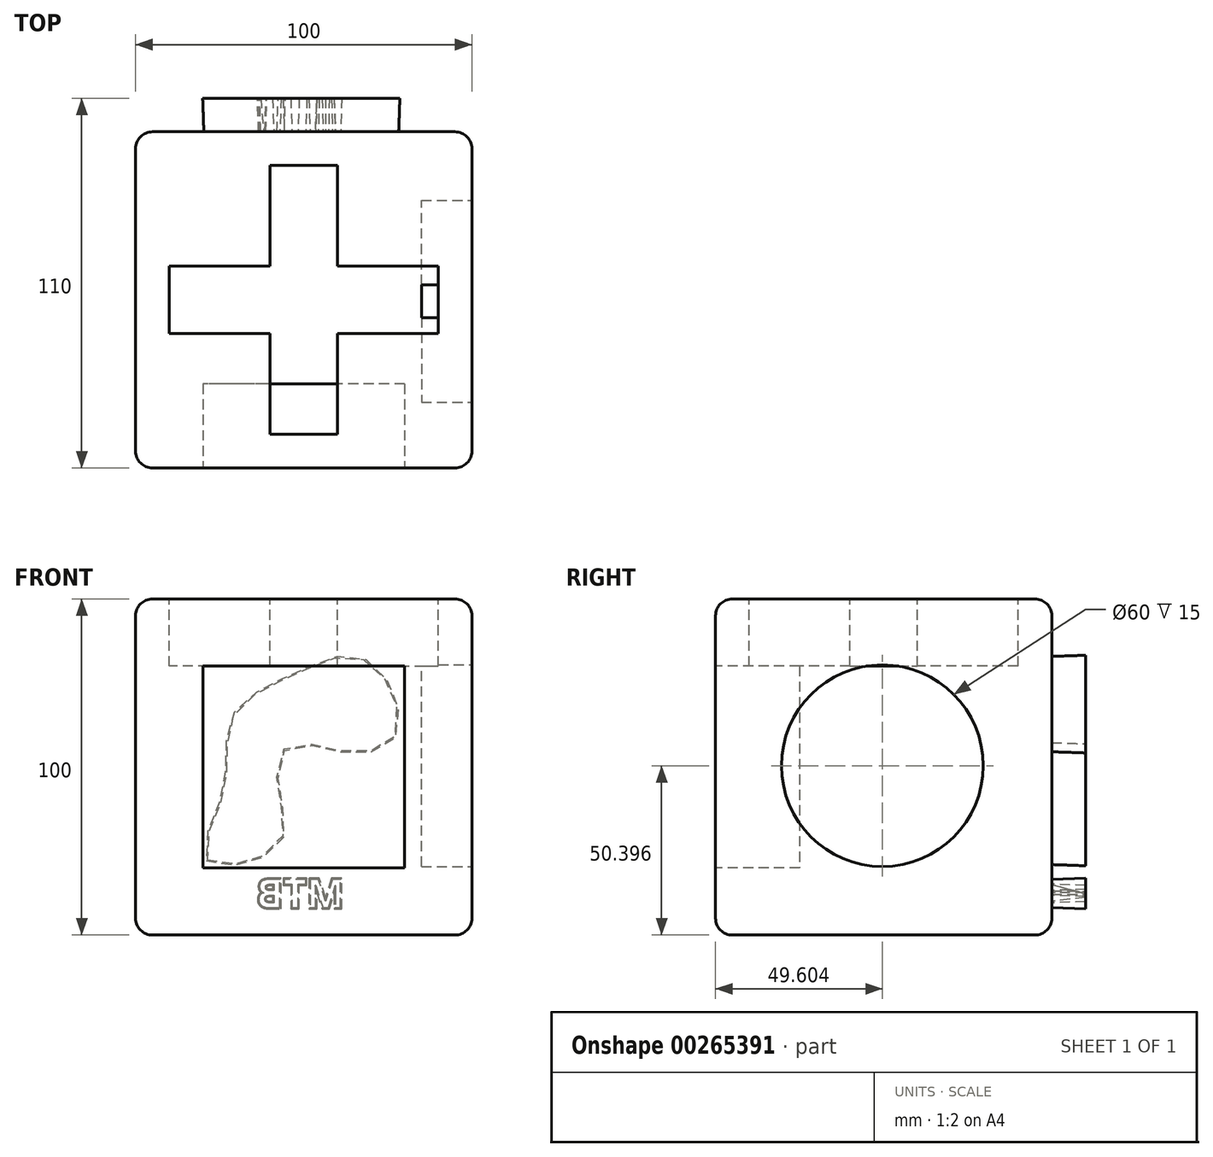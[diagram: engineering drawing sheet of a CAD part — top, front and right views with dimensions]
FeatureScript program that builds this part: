
annotation { "Feature Type Name" : "Feature", "Feature Type Description" : "" }
export const myFeature = defineFeature(function(context is Context, id is Id, definition is map)
    precondition{}
    {
        {
            var Q0;
            Q0=qCreatedBy(makeId("Front.planeOp"),FACE);
            var sketch = newSketch(context, id + "F0", { "sketchPlane" : qUnion([Q0])});
            skLineSegment(sketch, "E0.bottom", {"start": v(50, 50) * mm, "end": v(-50, 50) * mm});
            skLineSegment(sketch, "E0.top", {"start": v(50, -50) * mm, "end": v(-50, -50) * mm});
            skLineSegment(sketch, "E0.left", {"start": v(50, 50) * mm, "end": v(50, -50) * mm});
            skLineSegment(sketch, "E0.right", {"start": v(-50, 50) * mm, "end": v(-50, -50) * mm});
            skPoint(sketch, "E0.middle", {"position": v(0, 0) * mm});
            skSolve(sketch);
        }
        {
            var Q0;
            Q0=makeQuery(id+"F0.imprint","IMPRINT",FACE,{"disambiguationData":[TD([[makeQuery(id+"F0.imprint","IMPRINT",EDGE,{"derivedFrom":sQuery(id+"F0.wireOp",EDGE,"E0.bottom")}),1.0]])]});
            extrude(context, id + "F1", {"entities" : qUnion([Q0]), "depth" : 100 * mm});
        }
        {
            var Q0;
            Q0=makeQuery(id+"F1.opExtrude","CAP_FACE",FACE,{"disambiguationData":[OSD([sQuery(id+"F0.wireOp",EDGE,"E0.bottom"),sQuery(id+"F0.wireOp",EDGE,"E0.top"),sQuery(id+"F0.wireOp",EDGE,"E0.left"),sQuery(id+"F0.wireOp",EDGE,"E0.right")])],"isStart":false});
            var sketch = newSketch(context, id + "F2", { "sketchPlane" : qUnion([Q0])});
            skLineSegment(sketch, "E1.bottom", {"start": v(30, 30) * mm, "end": v(-30, 30) * mm});
            skLineSegment(sketch, "E1.top", {"start": v(30, -30) * mm, "end": v(-30, -30) * mm});
            skLineSegment(sketch, "E1.left", {"start": v(30, 30) * mm, "end": v(30, -30) * mm});
            skLineSegment(sketch, "E1.right", {"start": v(-30, 30) * mm, "end": v(-30, -30) * mm});
            skPoint(sketch, "E1.middle", {"position": v(0, 0) * mm});
            skSolve(sketch);
        }
        {
            var Q0;
            Q0 = qSketchRegion(id + "F2", true);
            extrude(context, id + "F3", {"entities" : qUnion([Q0]), "operationType" : NewBodyOperationType.REMOVE, "oppositeDirection" : true, "depth" : 25 * mm});
        }
        {
            var Q0;
            Q0=makeQuery(id+"F1.opExtrude","SWEPT_FACE",FACE,{"disambiguationData":[OSD([sQuery(id+"F0.wireOp",EDGE,"E0.left")])]});
            var sketch = newSketch(context, id + "F4", { "sketchPlane" : qUnion([Q0])});
            skLineSegment(sketch, "E2", {"start": v(-100, 50) * mm, "end": v(0, -50) * mm, "construction": true});
            skLineSegment(sketch, "E3", {"start": v(0, 50) * mm, "end": v(-101.6, -50) * mm, "construction": true});
            skCircle(sketch, "E4", {"center": v(-50.4, 0.4) * mm, "radius": 30 * mm});
            skSolve(sketch);
        }
        {
            var Q0;
            Q0 = qSketchRegion(id + "F4", true);
            extrude(context, id + "F5", {"entities" : qUnion([Q0]), "operationType" : NewBodyOperationType.REMOVE, "oppositeDirection" : true, "depth" : 15 * mm});
        }
        {
            var Q0;
            Q0=makeQuery(id+"F1.opExtrude","CAP_FACE",FACE,{"disambiguationData":[OSD([sQuery(id+"F0.wireOp",EDGE,"E0.bottom"),sQuery(id+"F0.wireOp",EDGE,"E0.top"),sQuery(id+"F0.wireOp",EDGE,"E0.left"),sQuery(id+"F0.wireOp",EDGE,"E0.right")])],"isStart":true});
            var sketch = newSketch(context, id + "F6", { "sketchPlane" : qUnion([Q0])});
            skFitSpline(sketch, "E5", {"points": [v(-25.94, 23.08) * mm, v(-15.32, 32.72) * mm, v(1.4, 28.08) * mm, v(21.06, 15.02) * mm, v(23.87, -7.57) * mm, v(28.75, -27.6) * mm, v(7.75, -23.32) * mm, v(7.75, -6.1) * mm, v(4.46, 6.6) * mm, v(-10.44, 5) * mm, v(-26.56, 8.18) * mm, v(-25.94, 23.08) * mm]});
            skText(sketch, "E6", { "text": "MTB", "fontName": "OpenSans-Bold.ttf"});
            const initialGuessF6  = {"E6": [-0.01203, -0.04188, 1, 0, 0.00855]};
            skSetInitialGuess(sketch, initialGuessF6);
            skSolve(sketch);
        }
        {
            var Q0;
            Q0 = qSketchRegion(id + "F6", true);
            extrude(context, id + "F7", {"entities" : qUnion([Q0]), "operationType" : NewBodyOperationType.ADD, "depth" : 10 * mm, "hasDraft" : true, "draftAngle" : 2 * degree});
        }
        {
            var Q0;
            Q0=makeQuery(id+"F1.opExtrude","SWEPT_FACE",FACE,{"disambiguationData":[OSD([sQuery(id+"F0.wireOp",EDGE,"E0.bottom")])]});
            var sketch = newSketch(context, id + "F8", { "sketchPlane" : qUnion([Q0])});
            skLineSegment(sketch, "E7", {"start": v(50, 0) * mm, "end": v(-50, -100) * mm, "construction": true});
            skLineSegment(sketch, "E8", {"start": v(-50, 0) * mm, "end": v(50, -100) * mm, "construction": true});
            skLineSegment(sketch, "E9.bottom", {"start": v(10, -10) * mm, "end": v(-10, -10) * mm});
            skLineSegment(sketch, "E9.top", {"start": v(10, -90) * mm, "end": v(-10, -90) * mm});
            skLineSegment(sketch, "E9.left", {"start": v(10, -10) * mm, "end": v(10, -40) * mm});
            skLineSegment(sketch, "E9.right", {"start": v(-10, -10) * mm, "end": v(-10, -40) * mm});
            skPoint(sketch, "E9.middle", {"position": v(0, -50) * mm});
            skLineSegment(sketch, "E10.top", {"start": v(40, -40) * mm, "end": v(10, -40) * mm});
            skLineSegment(sketch, "E10.left", {"start": v(40, -60) * mm, "end": v(40, -40) * mm});
            skLineSegment(sketch, "E10.right", {"start": v(-40, -60) * mm, "end": v(-40, -40) * mm});
            skLineSegment(sketch, "E11.trimOffspring", {"start": v(-10, -60) * mm, "end": v(-10, -90) * mm});
            skLineSegment(sketch, "E12.trimOffspring", {"start": v(-10, -40) * mm, "end": v(-40, -40) * mm});
            skLineSegment(sketch, "E13.trimOffspring", {"start": v(10, -60) * mm, "end": v(10, -90) * mm});
            skLineSegment(sketch, "E14.trimOffspring", {"start": v(-10, -60) * mm, "end": v(-40, -60) * mm});
            skLineSegment(sketch, "E15", {"start": v(10, -60) * mm, "end": v(40, -60) * mm});
            skSolve(sketch);
        }
        {
            var Q0;
            Q0=makeQuery(id+"F8.imprint","IMPRINT",FACE,{"disambiguationData":[TD([[makeQuery(id+"F8.imprint","IMPRINT",EDGE,{"derivedFrom":sQuery(id+"F8.wireOp",EDGE,"E9.bottom")}),1.0]])]});
            extrude(context, id + "F9", {"entities" : qUnion([Q0]), "operationType" : NewBodyOperationType.REMOVE, "oppositeDirection" : true, "depth" : 20 * mm});
        }
        {
            var Q0;
            Q0=makeQuery(id+"F1.opExtrude","CAP_EDGE",EDGE,{"disambiguationData":[OSD([sQuery(id+"F0.wireOp",EDGE,"E0.bottom")])],"isStart":true});
            var Q1;
            Q1=makeQuery(id+"F1.opExtrude","SWEPT_EDGE",EDGE,{"disambiguationData":[OSD([sQuery(id+"F0.wireOp",EDGE,"E0.bottom"),sQuery(id+"F0.wireOp",EDGE,"E0.left")])]});
            var Q2;
            Q2=makeQuery(id+"F1.opExtrude","CAP_EDGE",EDGE,{"disambiguationData":[OSD([sQuery(id+"F0.wireOp",EDGE,"E0.bottom")])],"isStart":false});
            var Q3;
            Q3=makeQuery(id+"F1.opExtrude","SWEPT_EDGE",EDGE,{"disambiguationData":[OSD([sQuery(id+"F0.wireOp",EDGE,"E0.bottom"),sQuery(id+"F0.wireOp",EDGE,"E0.right")])]});
            var Q4;
            Q4=makeQuery(id+"F1.opExtrude","CAP_EDGE",EDGE,{"disambiguationData":[OSD([sQuery(id+"F0.wireOp",EDGE,"E0.right")])],"isStart":false});
            var Q5;
            Q5=makeQuery(id+"F1.opExtrude","CAP_EDGE",EDGE,{"disambiguationData":[OSD([sQuery(id+"F0.wireOp",EDGE,"E0.left")])],"isStart":false});
            var Q6;
            Q6=makeQuery(id+"F1.opExtrude","CAP_EDGE",EDGE,{"disambiguationData":[OSD([sQuery(id+"F0.wireOp",EDGE,"E0.right")])],"isStart":true});
            var Q7;
            Q7=makeQuery(id+"F1.opExtrude","SWEPT_EDGE",EDGE,{"disambiguationData":[OSD([sQuery(id+"F0.wireOp",EDGE,"E0.top"),sQuery(id+"F0.wireOp",EDGE,"E0.right")])]});
            var Q8;
            Q8=makeQuery(id+"F1.opExtrude","CAP_EDGE",EDGE,{"disambiguationData":[OSD([sQuery(id+"F0.wireOp",EDGE,"E0.top")])],"isStart":false});
            var Q9;
            Q9=makeQuery(id+"F1.opExtrude","CAP_EDGE",EDGE,{"disambiguationData":[OSD([sQuery(id+"F0.wireOp",EDGE,"E0.top")])],"isStart":true});
            var Q10;
            Q10=makeQuery(id+"F1.opExtrude","SWEPT_EDGE",EDGE,{"disambiguationData":[OSD([sQuery(id+"F0.wireOp",EDGE,"E0.top"),sQuery(id+"F0.wireOp",EDGE,"E0.left")])]});
            var Q11;
            Q11=makeQuery(id+"F1.opExtrude","CAP_EDGE",EDGE,{"disambiguationData":[OSD([sQuery(id+"F0.wireOp",EDGE,"E0.left")])],"isStart":true});
            fillet(context, id + "F10", {"entities" : qUnion([Q0, Q1, Q2, Q3, Q4, Q5, Q6, Q7, Q8, Q9, Q10, Q11]), "radius" : 5 * mm, "tangentPropagation" : true, "allowEdgeOverflow" : false});
        }
    });
